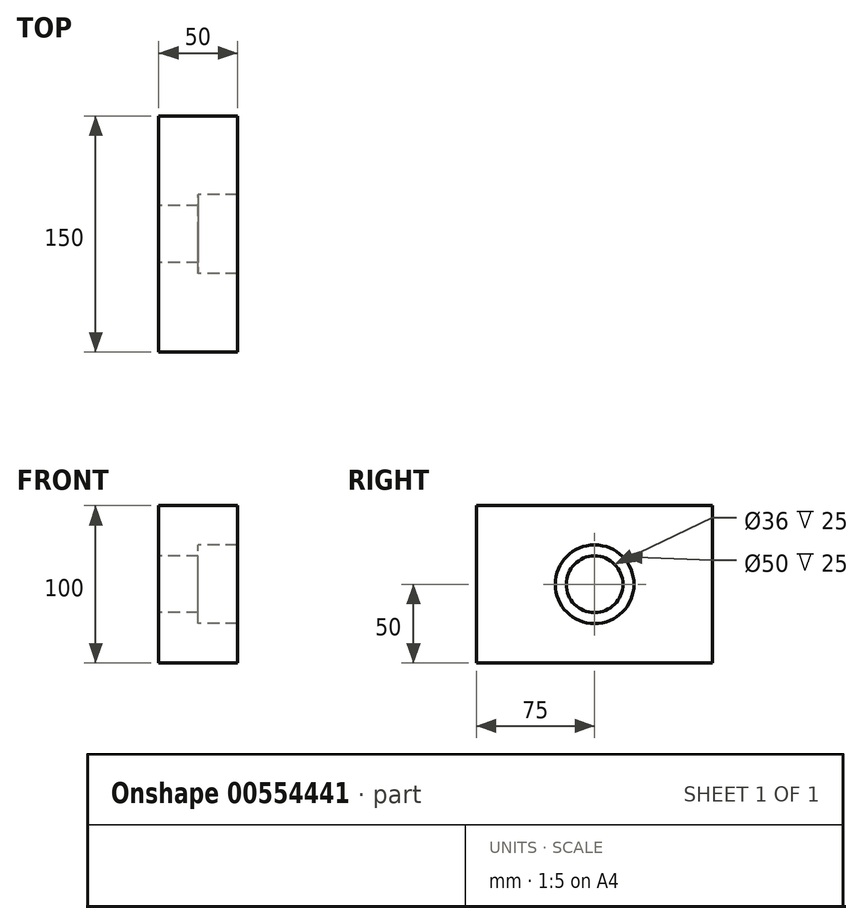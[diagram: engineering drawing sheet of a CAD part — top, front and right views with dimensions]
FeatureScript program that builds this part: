
annotation { "Feature Type Name" : "Feature", "Feature Type Description" : "" }
export const myFeature = defineFeature(function(context is Context, id is Id, definition is map)
    precondition{}
    {
        {
            var Q0;
            Q0=qCreatedBy(makeId("Right.planeOp"),FACE);
            var sketch = newSketch(context, id + "F0", { "sketchPlane" : qUnion([Q0])});
            skLineSegment(sketch, "E0.bottom", {"start": v(75, -50) * mm, "end": v(-75, -50) * mm});
            skLineSegment(sketch, "E0.top", {"start": v(75, 50) * mm, "end": v(-75, 50) * mm});
            skLineSegment(sketch, "E0.left", {"start": v(75, -50) * mm, "end": v(75, 50) * mm});
            skLineSegment(sketch, "E0.right", {"start": v(-75, -50) * mm, "end": v(-75, 50) * mm});
            skPoint(sketch, "E0.middle", {"position": v(0, 0) * mm});
            skCircle(sketch, "E1", {"center": v(0, 0) * mm, "radius": 18 * mm});
            skCircle(sketch, "E2", {"center": v(0, 0) * mm, "radius": 25 * mm});
            skSolve(sketch);
        }
        {
            var Q0;
            Q0=makeQuery(id+"F0.imprint","IMPRINT",FACE,{"disambiguationData":[TD([[makeQuery(id+"F0.imprint","IMPRINT",EDGE,{"derivedFrom":sQuery(id+"F0.wireOp",EDGE,"E0.bottom")}),-1.0]])]});
            var Q1;
            Q1=makeQuery(id+"F0.imprint","IMPRINT",FACE,{"disambiguationData":[TD([[makeQuery(id+"F0.imprint","IMPRINT",EDGE,{"derivedFrom":sQuery(id+"F0.wireOp",EDGE,"E1")}),-1.0]])]});
            extrude(context, id + "F1", {"entities" : qUnion([Q0, Q1]), "depth" : 25 * mm, "offsetDistance" : 25 * mm});
        }
        {
            var Q0;
            Q0 = qSketchRegion(id + "F0", true);
            extrude(context, id + "F2", {"entities" : qUnion([Q0]), "operationType" : NewBodyOperationType.ADD, "depth" : 50 * mm, "offsetDistance" : 25 * mm});
        }
    });
